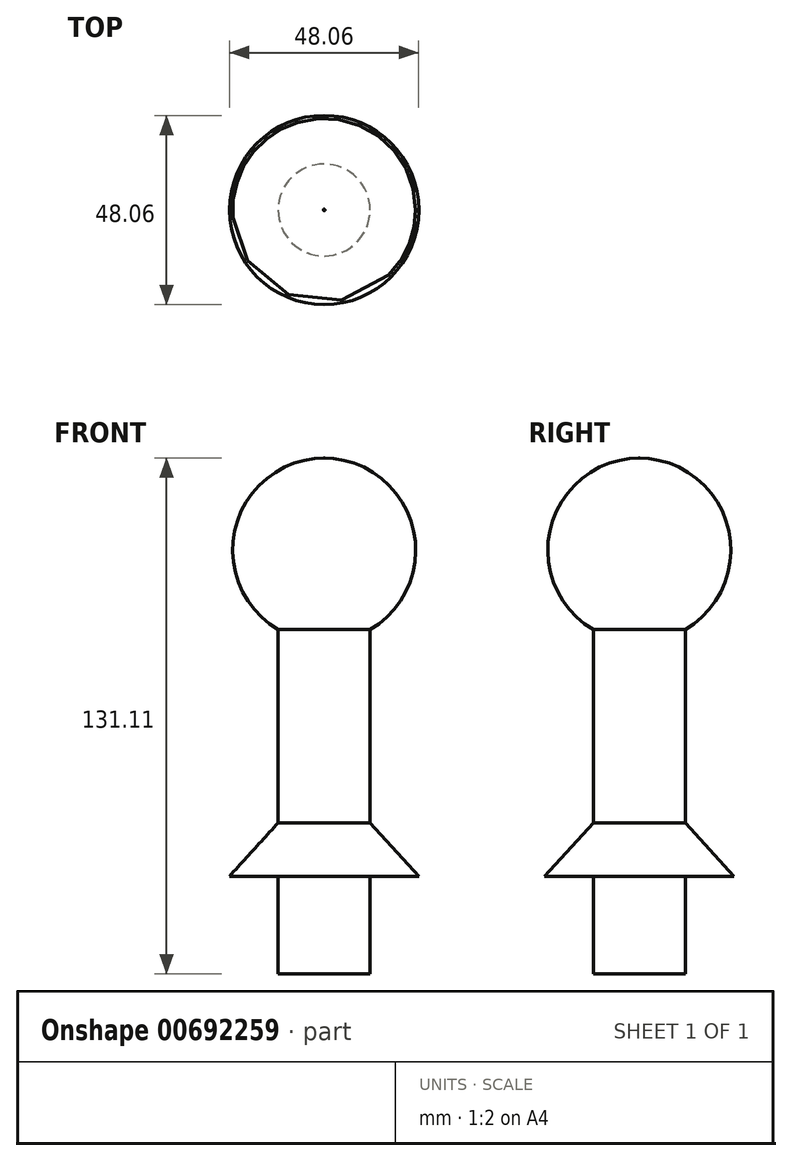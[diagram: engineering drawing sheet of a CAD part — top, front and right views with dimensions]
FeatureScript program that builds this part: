
annotation { "Feature Type Name" : "Feature", "Feature Type Description" : "" }
export const myFeature = defineFeature(function(context is Context, id is Id, definition is map)
    precondition{}
    {
        {
            var Q0;
            Q0=qCreatedBy(makeId("Front.planeOp"),FACE);
            var sketch = newSketch(context, id + "F0", { "sketchPlane" : qUnion([Q0])});
            skLineSegment(sketch, "E0", {"start": v(0, -91.93) * mm, "end": v(0, 92.64) * mm});
            skArc(sketch, "E1", {"start": v(0, 45.9) * mm, "mid": v(23.26, 69.27) * mm, "end": v(0, 92.64) * mm});
            skLineSegment(sketch, "E2", {"start": v(11.67, 49.08) * mm, "end": v(11.67, 0) * mm});
            skLineSegment(sketch, "E3", {"start": v(11.67, 0) * mm, "end": v(11.67, 0) * mm});
            skLineSegment(sketch, "E4", {"start": v(24.03, -13.6) * mm, "end": v(24.03, -13.6) * mm});
            skLineSegment(sketch, "E5", {"start": v(24.03, -13.6) * mm, "end": v(11.67, 0) * mm});
            skLineSegment(sketch, "E6", {"start": v(24.03, -13.6) * mm, "end": v(11.67, -13.6) * mm});
            skLineSegment(sketch, "E7", {"start": v(11.67, -13.6) * mm, "end": v(11.67, -38.47) * mm});
            skLineSegment(sketch, "E8", {"start": v(11.67, -38.47) * mm, "end": v(11.67, -38.47) * mm});
            skLineSegment(sketch, "E9", {"start": v(11.67, -38.47) * mm, "end": v(0, -38.47) * mm});
            skSolve(sketch);
        }
        {
            var Q0;
            Q0 = qSketchRegion(id + "F0", true);
            var Q1;
            {var subQ0=sQuery(id+"F0.wireOp",EDGE,"E1");var subQ1=sQuery(id+"F0.wireOp",EDGE,"E0");var subQ2=makeQuery(id+"F0.imprint","INTERSECT",VERTEX,{"disambiguationData":[OD(0.0)],"derivedFrom":[subQ1,subQ0]});Q1=makeQuery(id+"F0.imprint","IMPRINT",FACE,{"disambiguationData":[TD([[makeQuery(id+"F0.imprint","IMPRINT",EDGE,{"disambiguationData":[TD([[subQ2,1.0]])],"derivedFrom":subQ1}),-1.0]])]});}
            var Q2;
            Q2=sQuery(id+"F0.wireOp",EDGE,"E0");
            revolve(context, id + "F1", {"entities" : qUnion([Q0, Q1]), "axis" : qUnion([Q2]), "revolveType" : RevolveType.FULL});
        }
    });
